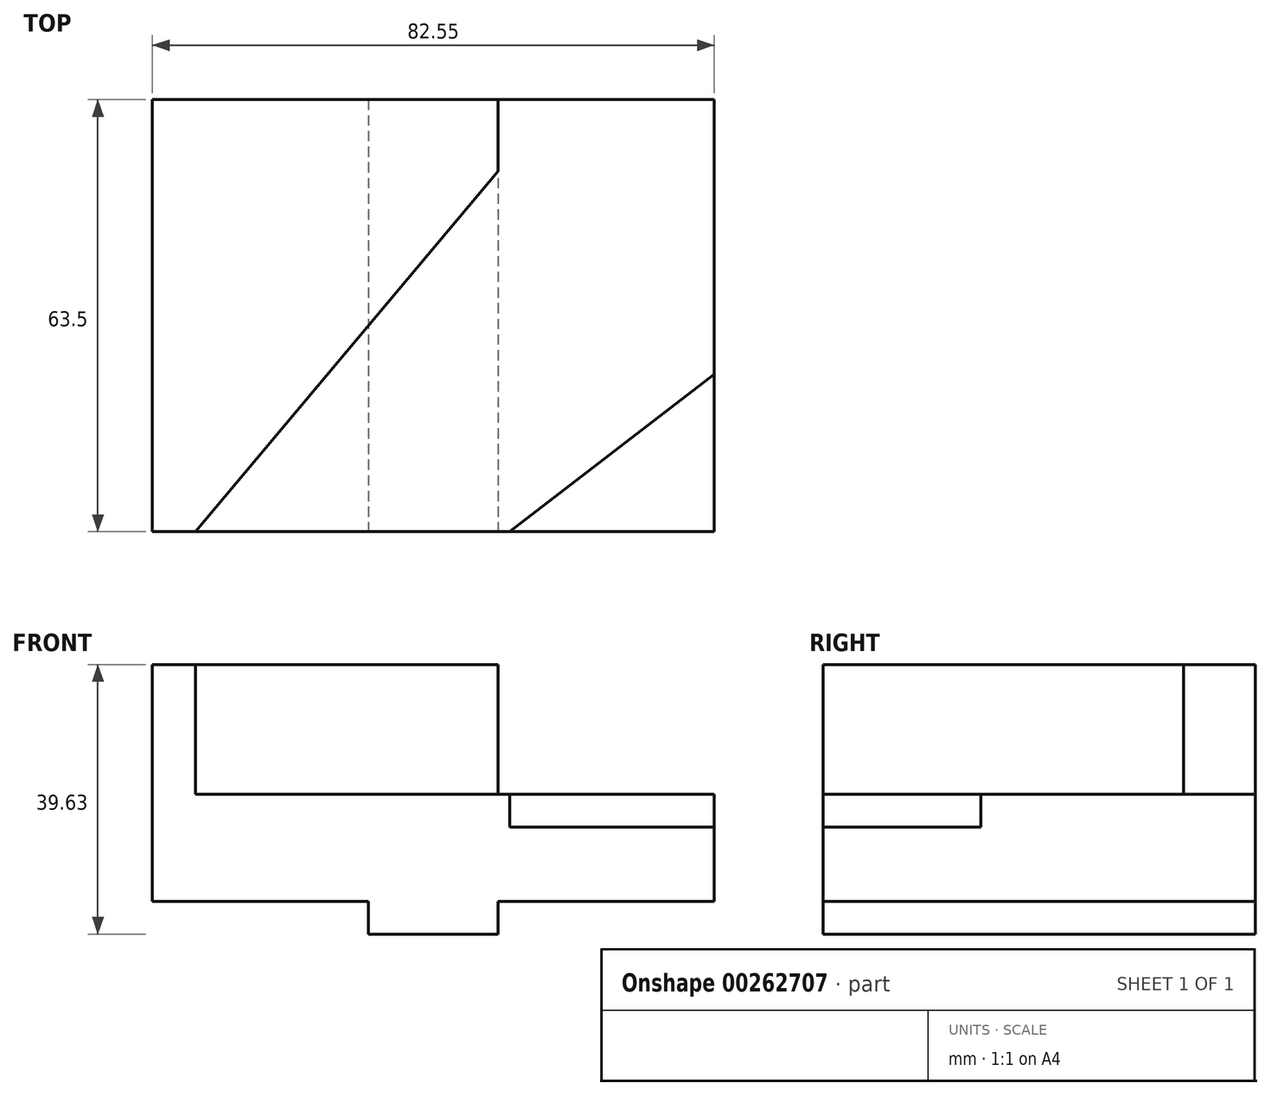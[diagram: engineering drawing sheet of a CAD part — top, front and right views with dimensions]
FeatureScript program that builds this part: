
annotation { "Feature Type Name" : "Feature", "Feature Type Description" : "" }
export const myFeature = defineFeature(function(context is Context, id is Id, definition is map)
    precondition{}
    {
        {
            var Q0;
            Q0=qCreatedBy(makeId("Front.planeOp"),FACE);
            var sketch = newSketch(context, id + "F0", { "sketchPlane" : qUnion([Q0])});
            skLineSegment(sketch, "E0.bottom", {"start": v(-46.34, 18.14) * mm, "end": v(36.21, 18.14) * mm});
            skLineSegment(sketch, "E0.top", {"start": v(-46.34, -21.49) * mm, "end": v(36.21, -21.49) * mm});
            skLineSegment(sketch, "E0.left", {"start": v(-46.34, 18.14) * mm, "end": v(-46.34, -21.49) * mm});
            skLineSegment(sketch, "E0.right", {"start": v(36.21, 18.14) * mm, "end": v(36.21, -21.49) * mm});
            skSolve(sketch);
        }
        {
            var Q0;
            Q0=makeQuery(id+"F0.imprint","IMPRINT",FACE,{"disambiguationData":[TD([[makeQuery(id+"F0.imprint","IMPRINT",EDGE,{"derivedFrom":sQuery(id+"F0.wireOp",EDGE,"E0.bottom")}),-1.0]])]});
            extrude(context, id + "F1", {"entities" : qUnion([Q0]), "oppositeDirection" : true, "depth" : 63.5 * mm});
        }
        {
            var Q0;
            Q0=makeQuery(id+"F1.opExtrude","CAP_FACE",FACE,{"disambiguationData":[OSD([sQuery(id+"F0.wireOp",EDGE,"E0.bottom"),sQuery(id+"F0.wireOp",EDGE,"E0.top"),sQuery(id+"F0.wireOp",EDGE,"E0.left"),sQuery(id+"F0.wireOp",EDGE,"E0.right")])],"isStart":true});
            var sketch = newSketch(context, id + "F2", { "sketchPlane" : qUnion([Q0])});
            skLineSegment(sketch, "E1.bottom", {"start": v(-46.34, -16.66) * mm, "end": v(-14.59, -16.66) * mm});
            skLineSegment(sketch, "E1.top", {"start": v(-46.34, -21.49) * mm, "end": v(-14.59, -21.49) * mm});
            skLineSegment(sketch, "E1.left", {"start": v(-46.34, -16.66) * mm, "end": v(-46.34, -21.49) * mm});
            skLineSegment(sketch, "E1.right", {"start": v(-14.59, -16.66) * mm, "end": v(-14.59, -21.49) * mm});
            skSolve(sketch);
        }
        {
            var Q0;
            Q0 = qSketchRegion(id + "F2", true);
            extrude(context, id + "F3", {"entities" : qUnion([Q0]), "operationType" : NewBodyOperationType.REMOVE, "oppositeDirection" : true, "depth" : 153.92 * mm});
        }
        {
            var Q0;
            Q0=makeQuery(id+"F1.opExtrude","CAP_FACE",FACE,{"disambiguationData":[OSD([sQuery(id+"F0.wireOp",EDGE,"E0.bottom"),sQuery(id+"F0.wireOp",EDGE,"E0.top"),sQuery(id+"F0.wireOp",EDGE,"E0.left"),sQuery(id+"F0.wireOp",EDGE,"E0.right")])],"isStart":true});
            var sketch = newSketch(context, id + "F4", { "sketchPlane" : qUnion([Q0])});
            skLineSegment(sketch, "E2.bottom", {"start": v(4.46, -16.66) * mm, "end": v(36.21, -16.66) * mm});
            skLineSegment(sketch, "E2.top", {"start": v(4.46, -21.49) * mm, "end": v(36.21, -21.49) * mm});
            skLineSegment(sketch, "E2.left", {"start": v(4.46, -16.66) * mm, "end": v(4.46, -21.49) * mm});
            skLineSegment(sketch, "E2.right", {"start": v(36.21, -16.66) * mm, "end": v(36.21, -21.49) * mm});
            skSolve(sketch);
        }
        {
            var Q0;
            Q0 = qSketchRegion(id + "F4", true);
            extrude(context, id + "F5", {"entities" : qUnion([Q0]), "operationType" : NewBodyOperationType.REMOVE, "oppositeDirection" : true, "depth" : 83.06 * mm});
        }
        {
            var Q0;
            Q0=makeQuery(id+"F1.opExtrude","SWEPT_FACE",FACE,{"disambiguationData":[OSD([sQuery(id+"F0.wireOp",EDGE,"E0.bottom")])]});
            var sketch = newSketch(context, id + "F6", { "sketchPlane" : qUnion([Q0])});
            skLineSegment(sketch, "E3", {"start": v(4.46, 63.5) * mm, "end": v(36.21, 63.5) * mm});
            skLineSegment(sketch, "E4", {"start": v(36.21, 63.5) * mm, "end": v(36.21, 0) * mm});
            skLineSegment(sketch, "E5", {"start": v(36.21, 0) * mm, "end": v(-39.99, 0) * mm});
            skLineSegment(sketch, "E6", {"start": v(-39.99, 0) * mm, "end": v(4.46, 52.97) * mm});
            skLineSegment(sketch, "E7", {"start": v(4.46, 52.97) * mm, "end": v(4.46, 63.5) * mm});
            skSolve(sketch);
        }
        {
            var Q0;
            Q0=makeQuery(id+"F6.imprint","IMPRINT",FACE,{"disambiguationData":[TD([[makeQuery(id+"F6.imprint","IMPRINT",EDGE,{"derivedFrom":sQuery(id+"F6.wireOp",EDGE,"E3")}),-1.0]])]});
            extrude(context, id + "F7", {"entities" : qUnion([Q0]), "operationType" : NewBodyOperationType.REMOVE, "oppositeDirection" : true, "depth" : 19.05 * mm});
        }
        {
            var Q0;
            Q0=makeQuery(id+"F7.boolean.opBoolean","COPY",FACE,{"derivedFrom":makeQuery(id+"F7.opExtrude","CAP_FACE",FACE,{"disambiguationData":[OSD([sQuery(id+"F6.wireOp",EDGE,"E3"),sQuery(id+"F6.wireOp",EDGE,"E4"),sQuery(id+"F6.wireOp",EDGE,"E5"),sQuery(id+"F6.wireOp",EDGE,"E6"),sQuery(id+"F6.wireOp",EDGE,"E7")])],"isStart":false})});
            var sketch = newSketch(context, id + "F8", { "sketchPlane" : qUnion([Q0])});
            skLineSegment(sketch, "E8", {"start": v(6.15, 0) * mm, "end": v(36.21, 23.16) * mm});
            skLineSegment(sketch, "E9", {"start": v(36.21, 23.16) * mm, "end": v(36.21, 0) * mm});
            skLineSegment(sketch, "E10", {"start": v(36.21, 0) * mm, "end": v(6.15, 0) * mm});
            skSolve(sketch);
        }
        {
            var Q0;
            Q0 = qSketchRegion(id + "F8", true);
            extrude(context, id + "F9", {"entities" : qUnion([Q0]), "operationType" : NewBodyOperationType.REMOVE, "oppositeDirection" : true, "depth" : 4.83 * mm});
        }
    });
